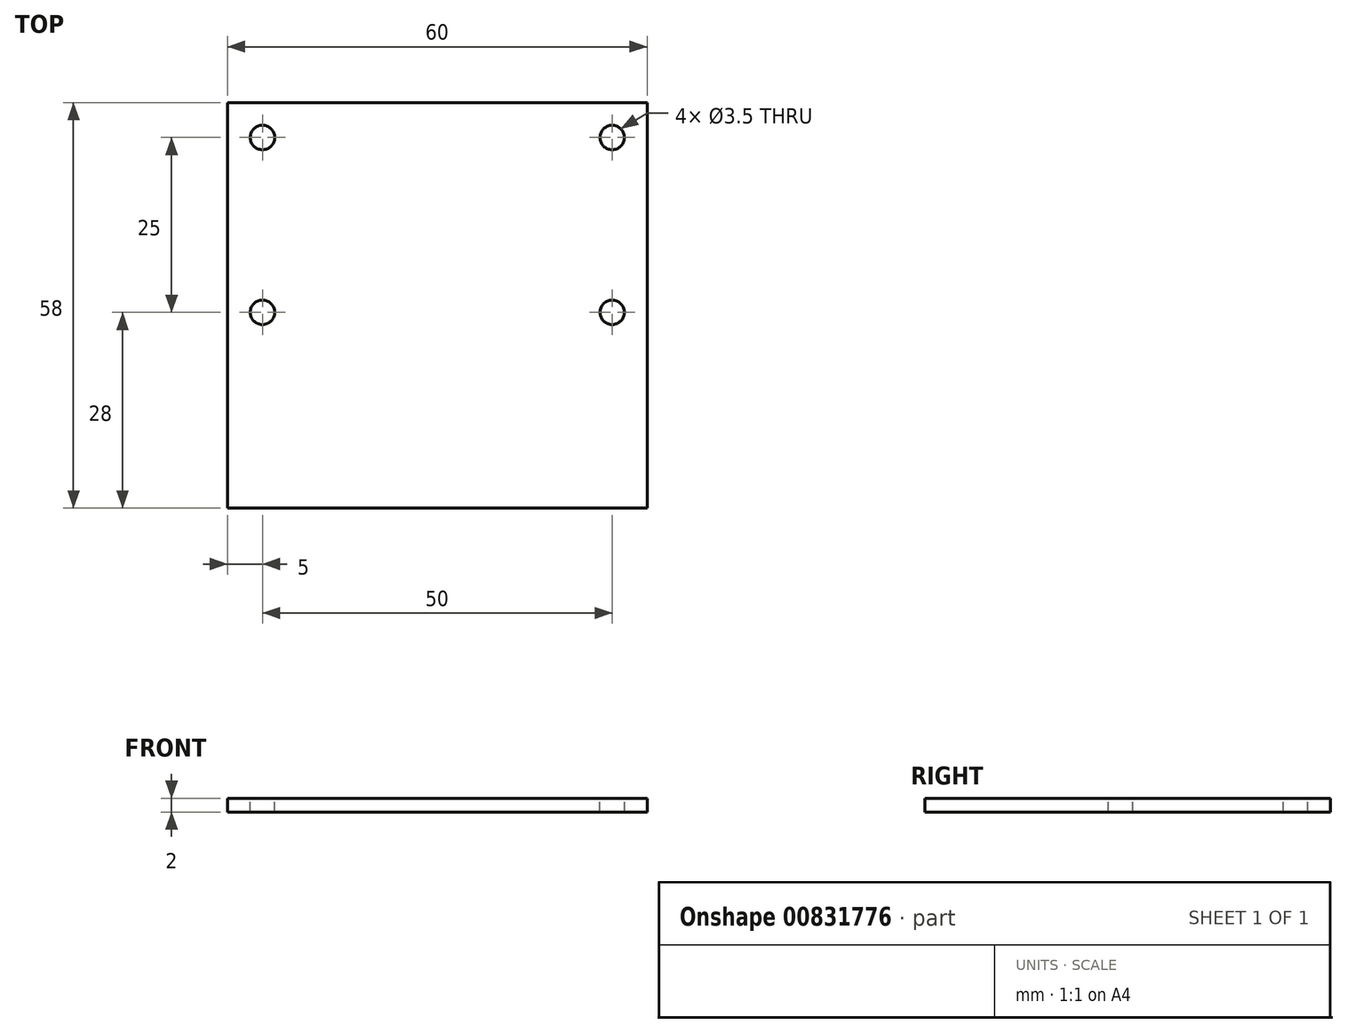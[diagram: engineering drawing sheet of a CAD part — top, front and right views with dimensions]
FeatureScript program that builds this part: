
annotation { "Feature Type Name" : "Feature", "Feature Type Description" : "" }
export const myFeature = defineFeature(function(context is Context, id is Id, definition is map)
    precondition{}
    {
        {
            var Q0;
            Q0=qCreatedBy(makeId("Top.planeOp"),FACE);
            var sketch = newSketch(context, id + "F0", { "sketchPlane" : qUnion([Q0])});
            skLineSegment(sketch, "E0.bottom", {"start": v(0, 0) * mm, "end": v(60, 0) * mm});
            skLineSegment(sketch, "E0.top", {"start": v(0, 58) * mm, "end": v(60, 58) * mm});
            skLineSegment(sketch, "E0.left", {"start": v(0, 0) * mm, "end": v(0, 58) * mm});
            skLineSegment(sketch, "E0.right", {"start": v(60, 0) * mm, "end": v(60, 58) * mm});
            skSolve(sketch);
        }
        {
            var Q0;
            Q0=makeQuery(id+"F0.imprint","IMPRINT",FACE,{"disambiguationData":[TD([[makeQuery(id+"F0.imprint","IMPRINT",EDGE,{"derivedFrom":sQuery(id+"F0.wireOp",EDGE,"E0.bottom")}),1.0]])]});
            extrude(context, id + "F1", {"entities" : qUnion([Q0]), "depth" : 2 * mm, "offsetDistance" : 25 * mm});
        }
        {
            var Q0;
            Q0=makeQuery(id+"F1.opExtrude","CAP_FACE",FACE,{"disambiguationData":[OSD([sQuery(id+"F0.wireOp",EDGE,"E0.bottom"),sQuery(id+"F0.wireOp",EDGE,"E0.top"),sQuery(id+"F0.wireOp",EDGE,"E0.left"),sQuery(id+"F0.wireOp",EDGE,"E0.right")])],"isStart":false});
            var sketch = newSketch(context, id + "F2", { "sketchPlane" : qUnion([Q0])});
            skCircle(sketch, "E1", {"center": v(5, 53) * mm, "radius": 1.75 * mm});
            skCircle(sketch, "E2", {"center": v(55, 53) * mm, "radius": 1.75 * mm});
            skCircle(sketch, "E3", {"center": v(55, 28) * mm, "radius": 1.75 * mm});
            skCircle(sketch, "E4", {"center": v(5, 28) * mm, "radius": 1.75 * mm});
            skLineSegment(sketch, "E5", {"start": v(5, 53) * mm, "end": v(55, 53) * mm, "construction": true});
            skLineSegment(sketch, "E6", {"start": v(55, 53) * mm, "end": v(55, 28) * mm, "construction": true});
            skLineSegment(sketch, "E7", {"start": v(55, 28) * mm, "end": v(5, 28) * mm, "construction": true});
            skLineSegment(sketch, "E8", {"start": v(5, 28) * mm, "end": v(5, 53) * mm, "construction": true});
            skSolve(sketch);
        }
        {
            var Q0;
            Q0=makeQuery(id+"F2.imprint","IMPRINT",FACE,{"disambiguationData":[TD([[makeQuery(id+"F2.imprint","IMPRINT",EDGE,{"derivedFrom":sQuery(id+"F2.wireOp",EDGE,"E1")}),1.0]])]});
            var Q1;
            Q1=makeQuery(id+"F2.imprint","IMPRINT",FACE,{"disambiguationData":[TD([[makeQuery(id+"F2.imprint","IMPRINT",EDGE,{"derivedFrom":sQuery(id+"F2.wireOp",EDGE,"E4")}),1.0]])]});
            var Q2;
            Q2=makeQuery(id+"F2.imprint","IMPRINT",FACE,{"disambiguationData":[TD([[makeQuery(id+"F2.imprint","IMPRINT",EDGE,{"derivedFrom":sQuery(id+"F2.wireOp",EDGE,"E3")}),1.0]])]});
            var Q3;
            Q3=makeQuery(id+"F2.imprint","IMPRINT",FACE,{"disambiguationData":[TD([[makeQuery(id+"F2.imprint","IMPRINT",EDGE,{"derivedFrom":sQuery(id+"F2.wireOp",EDGE,"E2")}),1.0]])]});
            extrude(context, id + "F3", {"entities" : qUnion([Q0, Q1, Q2, Q3]), "operationType" : NewBodyOperationType.REMOVE, "endBound" : BoundingType.THROUGH_ALL, "oppositeDirection" : true, "depth" : 25 * mm, "offsetDistance" : 25 * mm});
        }
    });
